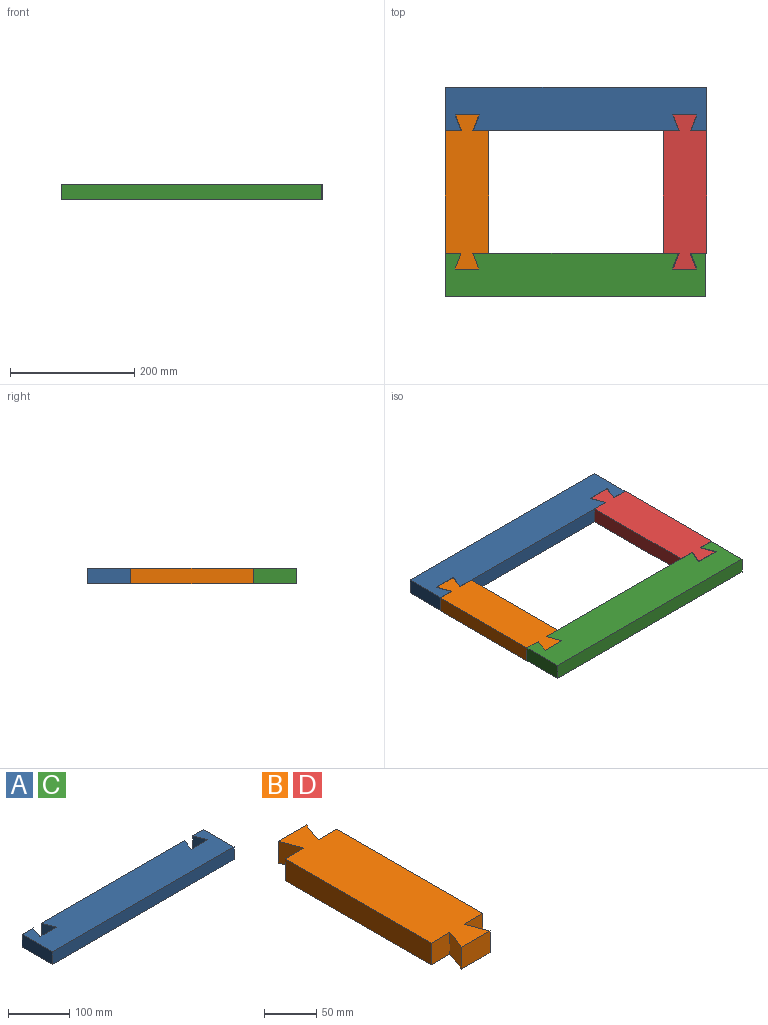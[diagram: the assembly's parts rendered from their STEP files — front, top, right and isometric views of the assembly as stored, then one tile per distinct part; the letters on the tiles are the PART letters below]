
ASSEMBLY  parts=4 mates=6
PART A: 14 faces, bbox 419.1x69.9x25.4 mm
  f0: plane 25.4x25.4mm, normal (0,1,0), area 645.2mm2, adj f1,f11,f12,f13
  f1: plane 69.85x25.4mm, normal (-1,0,0), area 1774.2mm2, adj f0,f2,f12,f13
  f2: plane 419.1x25.4mm, normal (0,-1,0), area 10645.1mm2, adj f1,f3,f12,f13
  f3: plane 69.85x25.4mm, normal (1,0,0), area 1774.2mm2, adj f2,f4,f12,f13
  f4: plane 25.4x25.4mm, normal (0,1,0), area 645.2mm2, adj f3,f5,f12,f13
  f5: plane 25.4x25.4mm, normal (-0.94,-0.35,0), area 689mm2, adj f4,f6,f12,f13
  f6: plane 38.1x25.4mm, normal (0,1,0), area 967.7mm2, adj f5,f7,f12,f13
  f7: plane 25.4x25.4mm, normal (0.94,-0.35,0), area 689mm2, adj f6,f8,f12,f13
  f8: plane 330.2x25.4mm, normal (0,1,0), area 8387.1mm2, adj f7,f9,f12,f13
  f9: plane 25.4x25.4mm, normal (-0.94,-0.35,0), area 689mm2, adj f8,f10,f12,f13
  f10: plane 38.1x25.4mm, normal (0,1,0), area 967.7mm2, adj f9,f11,f12,f13
  f11: plane 25.4x25.4mm, normal (0.94,-0.35,0), area 689mm2, adj f0,f10,f12,f13
  f12: plane 419.1x69.85mm, normal (0,0,1), area 27822.5mm2, adj f0,f1,f2,f3,f4,f5,f6,f7
  f13: plane 419.1x69.85mm, normal (0,0,-1), area 27822.5mm2, adj f0,f1,f2,f3,f4,f5,f6,f7
PART B: 14 faces, bbox 69.9x247.7x25.4 mm
  f0: plane 25.4x25.4mm, normal (0.94,0.35,0), area 689mm2, adj f1,f11,f12,f13
  f1: plane 25.4x25.4mm, normal (0,-1,0), area 645.2mm2, adj f0,f2,f12,f13
  f2: plane 196.85x25.4mm, normal (1,0,0), area 5000mm2, adj f1,f3,f12,f13
  f3: plane 25.4x25.4mm, normal (0,1,0), area 645.2mm2, adj f2,f4,f12,f13
  f4: plane 25.4x25.4mm, normal (0.94,-0.35,0), area 689mm2, adj f3,f5,f12,f13
  f5: plane 38.1x25.4mm, normal (0,1,0), area 967.7mm2, adj f4,f6,f12,f13
  f6: plane 25.4x25.4mm, normal (-0.94,-0.35,0), area 689mm2, adj f5,f7,f12,f13
  f7: plane 25.4x25.4mm, normal (0,1,0), area 645.2mm2, adj f6,f8,f12,f13
  f8: plane 196.85x25.4mm, normal (-1,0,0), area 5000mm2, adj f7,f9,f12,f13
  f9: plane 25.4x25.4mm, normal (0,-1,0), area 645.2mm2, adj f8,f10,f12,f13
  f10: plane 25.4x25.4mm, normal (-0.94,0.35,0), area 689mm2, adj f9,f11,f12,f13
  f11: plane 38.1x25.4mm, normal (0,-1,0), area 967.7mm2, adj f0,f10,f12,f13
  f12: plane 247.65x69.85mm, normal (0,0,1), area 15201.6mm2, adj f0,f1,f2,f3,f4,f5,f6,f7
  f13: plane 247.65x69.85mm, normal (0,0,-1), area 15201.6mm2, adj f0,f1,f2,f3,f4,f5,f6,f7
PART C: same geometry as A
PART D: same geometry as B
PLACE A rot(axis=(1,0,0),180deg) t=(-56.11,-153.68,-126.99)mm
PLACE B t=(-22.06,-252.1,-152.39)mm
PLACE C t=(-56.98,-350.53,-152.39)mm
PLACE D t=(328.65,-252.1,-152.39)mm
MATE planar D.f12 <-> C.f12  axis (0,0,1) through (328.65,-252.1,-126.99)mm
MATE planar B.f11 <-> C.f10  axis (0,-1,0) through (-22.06,-375.93,-139.69)mm
MATE planar D.f11 <-> C.f10  axis (0,-1,0) through (328.65,-375.93,-139.69)mm
MATE planar B.f12 <-> A.f13  axis (0,0,1) through (-22.06,-252.1,-126.99)mm
MATE planar D.f5 <-> A.f10  axis (0,1,0) through (328.65,-128.28,-139.69)mm
MATE planar A.f13 <-> D.f12  axis (0,0,1) through (153.44,-117.67,-126.99)mm
